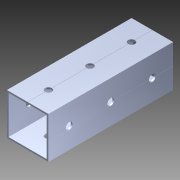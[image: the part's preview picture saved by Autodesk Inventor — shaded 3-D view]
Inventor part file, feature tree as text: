
AUTODESK INVENTOR PART (.ipt)
format: ipt  version: 2014 SP1 (Build 180222100, 222)  size: 1,242,624 bytes
history: native  units: in
note: dims shown in document units (in); Inventor stores cm internally (conversion verified against a paired STEP export)
features: extrude x4, sketch x4, pattern_circular x1, other x1, imported_body x1
ambient origin geometry x8: Origin, YZ Plane, XZ Plane, XY Plane, X Axis, Y Axis, Z Axis, Center Point
bodies: Body1 (feature_tree)
feature tree (11):
  pattern_circular  "CirPattern2"
  other  "1x1 tube1"
  extrude  "Extrusion1"  Depth=4.0in TaperAngle=0.0deg
  extrude  "Extrusion2"  Depth=1.0in TaperAngle=0.0deg
  extrude  "Extrusion3"  [1 undecoded]
  extrude  "Extrusion4"  [1 undecoded]
  imported_body  "Base1"
  sketch  "Sketch1"  dims[d0=50.0in d1=0.0in d2=4.0in d3=0.0in]
  sketch  "Sketch3"  dims[d4=1.0in d5=0.0in d6=1.0in d7=0.0in]
  sketch  "Sketch4"
  sketch  "Sketch5"
note: 2 required parameter values undecoded (feature->parameter linkage not recoverable at this tier; creation-order binding heuristic only, values carry confidence <= 0.55)
